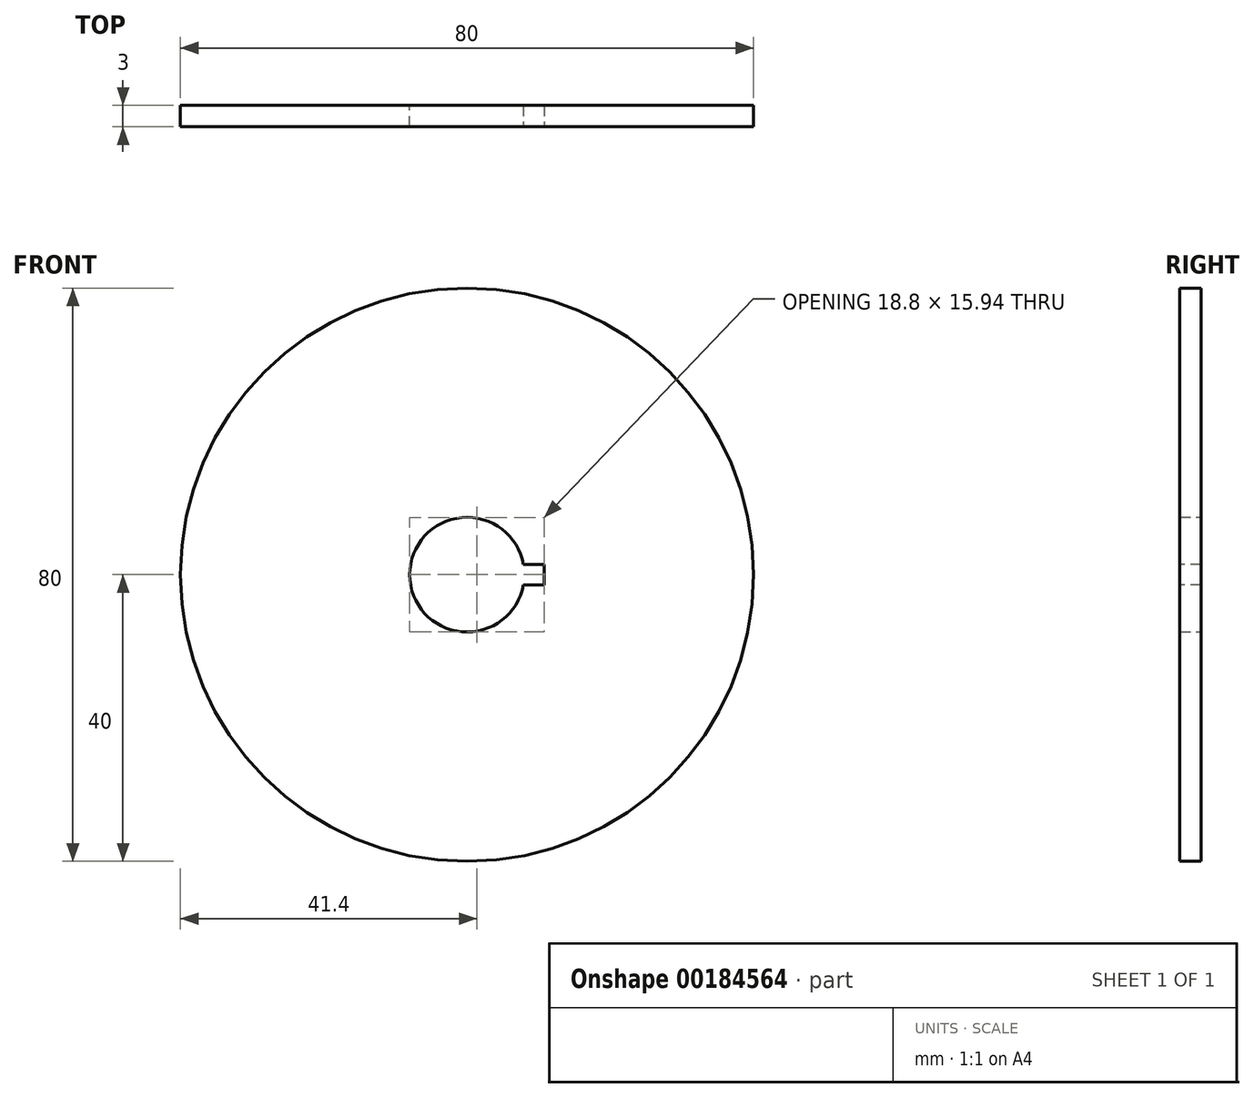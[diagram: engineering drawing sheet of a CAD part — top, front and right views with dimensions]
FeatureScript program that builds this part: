
annotation { "Feature Type Name" : "Feature", "Feature Type Description" : "" }
export const myFeature = defineFeature(function(context is Context, id is Id, definition is map)
    precondition{}
    {
        {
            var Q0;
            Q0=qCreatedBy(makeId("Front.planeOp"),FACE);
            var sketch = newSketch(context, id + "F0", { "sketchPlane" : qUnion([Q0])});
            skCircle(sketch, "E0", {"center": v(0, 0) * mm, "radius": 40 * mm});
            skCircle(sketch, "E1", {"center": v(0, 0) * mm, "radius": 8 * mm});
            skSolve(sketch);
        }
        {
            var Q0;
            Q0=makeQuery(id+"F0.imprint","IMPRINT",FACE,{"disambiguationData":[TD([[makeQuery(id+"F0.imprint","IMPRINT",EDGE,{"derivedFrom":sQuery(id+"F0.wireOp",EDGE,"E0")}),1.0]])]});
            extrude(context, id + "F1", {"entities" : qUnion([Q0]), "depth" : 3 * mm});
        }
        {
            var Q0;
            Q0=makeQuery(id+"F1.opExtrude","CAP_FACE",FACE,{"disambiguationData":[OSD([sQuery(id+"F0.wireOp",EDGE,"E0"),sQuery(id+"F0.wireOp",EDGE,"E1")])],"isStart":false});
            var sketch = newSketch(context, id + "F2", { "sketchPlane" : qUnion([Q0])});
            skLineSegment(sketch, "E2.bottom", {"start": v(10.8, 1.4) * mm, "end": v(5.2, 1.4) * mm});
            skLineSegment(sketch, "E2.top", {"start": v(10.8, -1.4) * mm, "end": v(5.2, -1.4) * mm});
            skLineSegment(sketch, "E2.left", {"start": v(10.8, 1.4) * mm, "end": v(10.8, -1.4) * mm});
            skLineSegment(sketch, "E2.right", {"start": v(5.2, 1.4) * mm, "end": v(5.2, -1.4) * mm});
            skPoint(sketch, "E2.middle", {"position": v(8, 0) * mm});
            skSolve(sketch);
        }
        {
            var Q0;
            {var subQ0=sQuery(id+"F2.wireOp",EDGE,"E2.left");Q0=makeQuery(id+"F2.imprint","IMPRINT",FACE,{"disambiguationData":[TD([[makeQuery(id+"F2.imprint","IMPRINT",EDGE,{"derivedFrom":subQ0}),-1.0]])]});}
            extrude(context, id + "F3", {"entities" : qUnion([Q0]), "operationType" : NewBodyOperationType.REMOVE, "endBound" : BoundingType.UP_TO_NEXT, "oppositeDirection" : true, "depth" : 25.4 * mm});
        }
    });
